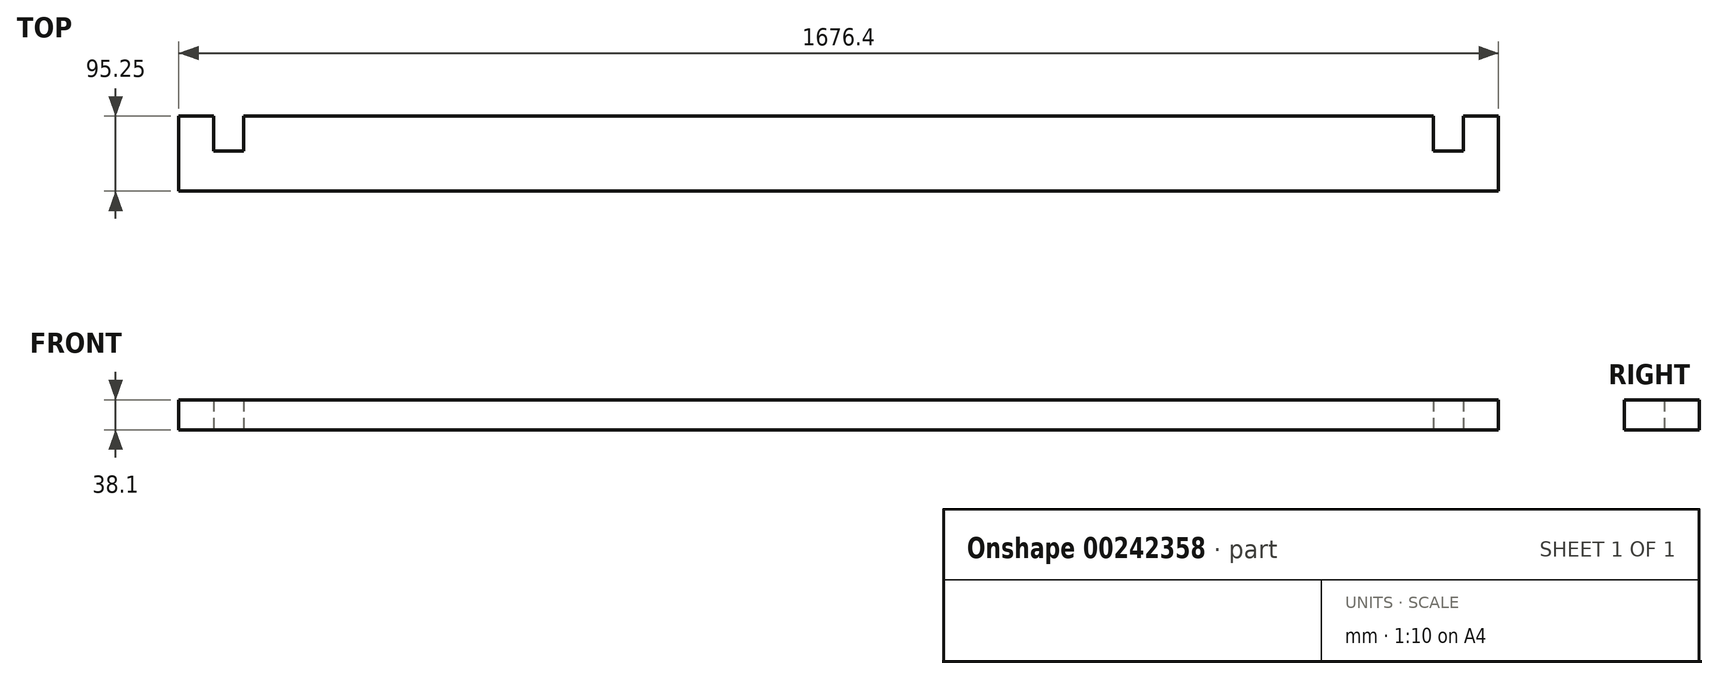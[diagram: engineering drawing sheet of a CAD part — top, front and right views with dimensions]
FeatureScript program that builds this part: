
annotation { "Feature Type Name" : "Feature", "Feature Type Description" : "" }
export const myFeature = defineFeature(function(context is Context, id is Id, definition is map)
    precondition{}
    {
        {
            var Q0;
            Q0=qCreatedBy(makeId("Top.planeOp"),FACE);
            var sketch = newSketch(context, id + "F0", { "sketchPlane" : qUnion([Q0])});
            skLineSegment(sketch, "E0.bottom", {"start": v(0, 0) * mm, "end": v(1676.4, 0) * mm});
            skLineSegment(sketch, "E0.top", {"start": v(0, 95.25) * mm, "end": v(1676.4, 95.25) * mm});
            skLineSegment(sketch, "E0.left", {"start": v(0, 0) * mm, "end": v(0, 95.25) * mm});
            skLineSegment(sketch, "E0.right", {"start": v(1676.4, 0) * mm, "end": v(1676.4, 95.25) * mm});
            skLineSegment(sketch, "E1.bottom", {"start": v(1631.95, 95.25) * mm, "end": v(1593.85, 95.25) * mm});
            skLineSegment(sketch, "E1.top", {"start": v(1631.95, 50.8) * mm, "end": v(1593.85, 50.8) * mm});
            skLineSegment(sketch, "E1.left", {"start": v(1593.85, 95.25) * mm, "end": v(1593.85, 50.8) * mm});
            skLineSegment(sketch, "E1.right", {"start": v(1631.95, 95.25) * mm, "end": v(1631.95, 50.8) * mm});
            skLineSegment(sketch, "E2.bottom", {"start": v(82.55, 95.25) * mm, "end": v(44.45, 95.25) * mm});
            skLineSegment(sketch, "E2.top", {"start": v(82.55, 50.8) * mm, "end": v(44.45, 50.8) * mm});
            skLineSegment(sketch, "E2.left", {"start": v(82.55, 95.25) * mm, "end": v(82.55, 50.8) * mm});
            skLineSegment(sketch, "E2.right", {"start": v(44.45, 95.25) * mm, "end": v(44.45, 50.8) * mm});
            skLineSegment(sketch, "E3", {"start": v(44.45, 95.25) * mm, "end": v(0, 95.25) * mm, "construction": true});
            skLineSegment(sketch, "E4", {"start": v(82.55, 95.25) * mm, "end": v(1593.85, 95.25) * mm, "construction": true});
            skLineSegment(sketch, "E5", {"start": v(1631.95, 95.25) * mm, "end": v(1676.4, 95.25) * mm, "construction": true});
            skSolve(sketch);
        }
        {
            var Q0;
            Q0=makeQuery(id+"F0.imprint","IMPRINT",FACE,{"disambiguationData":[TD([[makeQuery(id+"F0.imprint","IMPRINT",EDGE,{"derivedFrom":sQuery(id+"F0.wireOp",EDGE,"E0.bottom")}),1.0]])]});
            extrude(context, id + "F1", {"entities" : qUnion([Q0]), "depth" : 38.1 * mm});
        }
    });
